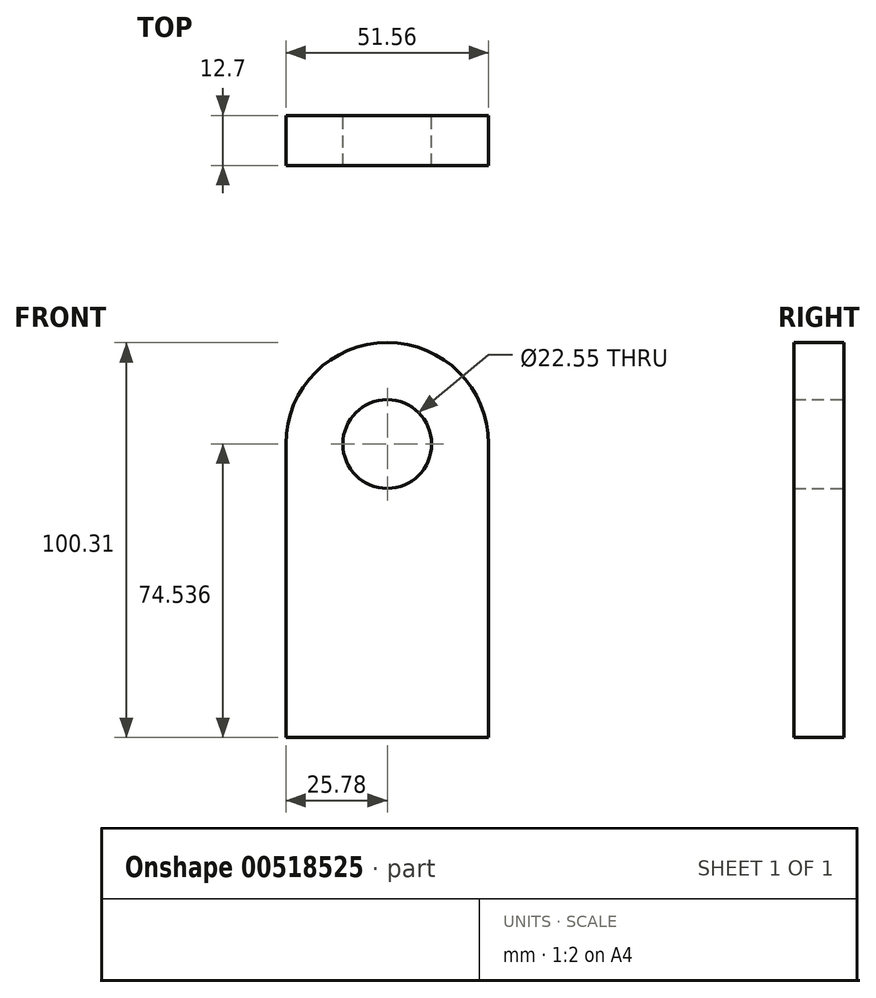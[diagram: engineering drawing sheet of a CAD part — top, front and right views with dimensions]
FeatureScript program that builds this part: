
annotation { "Feature Type Name" : "Feature", "Feature Type Description" : "" }
export const myFeature = defineFeature(function(context is Context, id is Id, definition is map)
    precondition{}
    {
        {
            var Q0;
            Q0=qCreatedBy(makeId("Front.planeOp"),FACE);
            var sketch = newSketch(context, id + "F0", { "sketchPlane" : qUnion([Q0])});
            skLineSegment(sketch, "E0.bottom", {"start": v(25.78, -37.27) * mm, "end": v(-25.78, -37.27) * mm});
            skLineSegment(sketch, "E0.left", {"start": v(25.78, -37.27) * mm, "end": v(25.78, 37.27) * mm});
            skLineSegment(sketch, "E0.right", {"start": v(-25.78, -37.27) * mm, "end": v(-25.78, 37.27) * mm});
            skPoint(sketch, "E0.middle", {"position": v(0, 0) * mm});
            skArc(sketch, "E1", {"start": v(25.78, 37.27) * mm, "mid": v(0, 63.04) * mm, "end": v(-25.78, 37.27) * mm});
            skCircle(sketch, "E2", {"center": v(0, 37.27) * mm, "radius": 11.28 * mm});
            skSolve(sketch);
        }
        {
            var Q0;
            Q0=makeQuery(id+"F0.imprint","IMPRINT",FACE,{"disambiguationData":[TD([[makeQuery(id+"F0.imprint","IMPRINT",EDGE,{"derivedFrom":sQuery(id+"F0.wireOp",EDGE,"E0.bottom")}),-1.0]])]});
            extrude(context, id + "F1", {"entities" : qUnion([Q0]), "depth" : 12.7 * mm, "offsetDistance" : 25.4 * mm});
        }
    });
